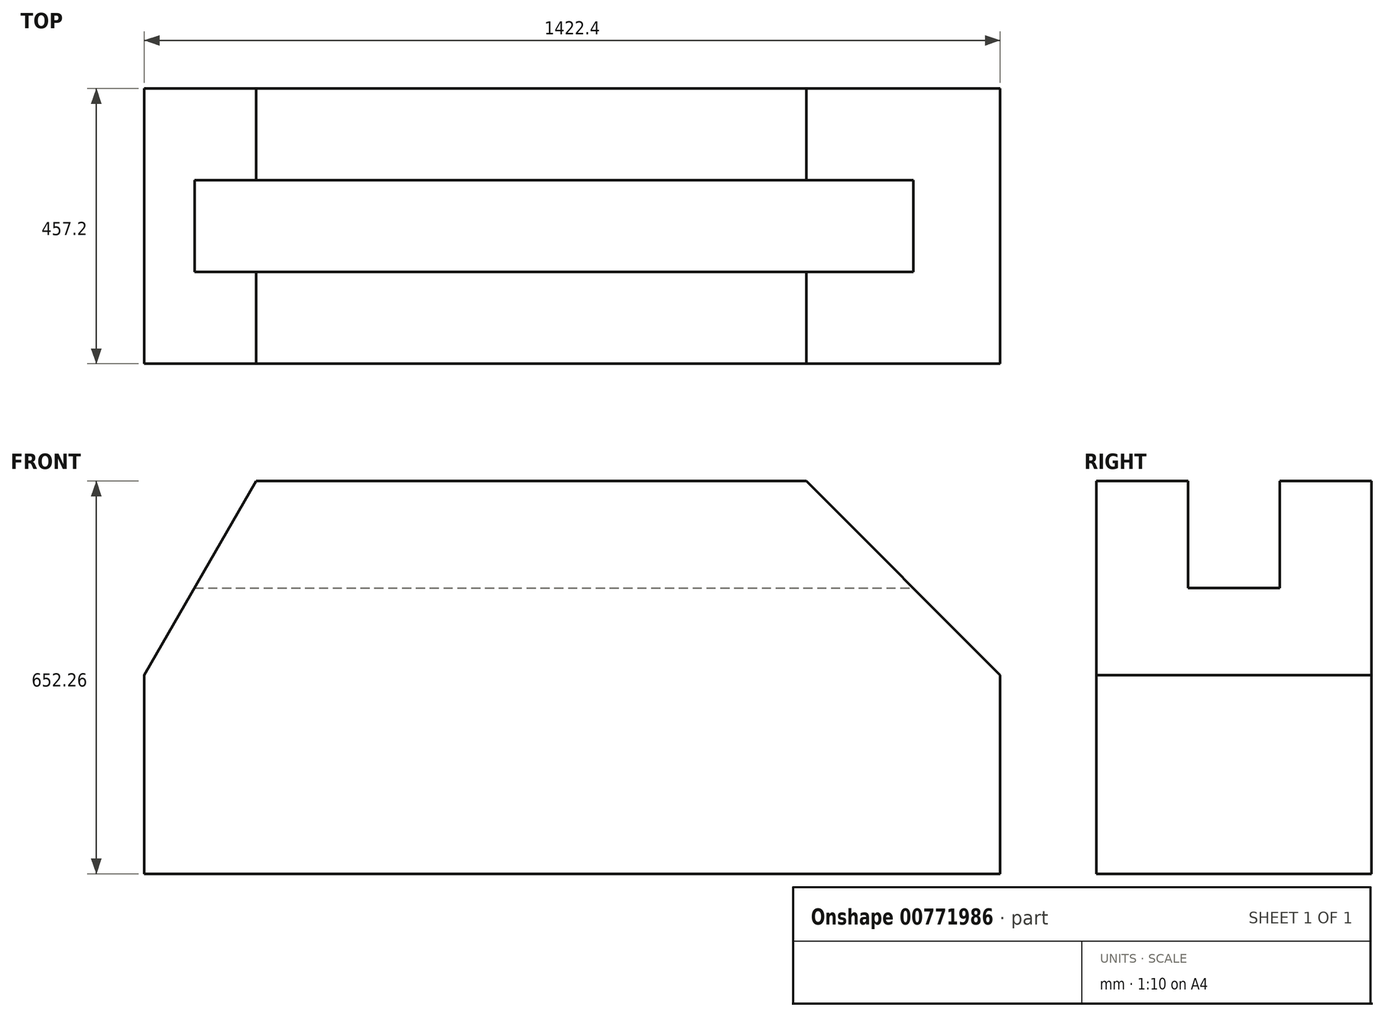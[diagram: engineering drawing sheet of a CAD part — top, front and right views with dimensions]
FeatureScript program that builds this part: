
annotation { "Feature Type Name" : "Feature", "Feature Type Description" : "" }
export const myFeature = defineFeature(function(context is Context, id is Id, definition is map)
    precondition{}
    {
        {
            var Q0;
            Q0=qCreatedBy(makeId("Front.planeOp"),FACE);
            var sketch = newSketch(context, id + "F0", { "sketchPlane" : qUnion([Q0])});
            skLineSegment(sketch, "E0", {"start": v(0, 0) * mm, "end": v(1422.4, 0) * mm});
            skLineSegment(sketch, "E1", {"start": v(1422.4, 0) * mm, "end": v(1422.4, 330.2) * mm});
            skLineSegment(sketch, "E2", {"start": v(1422.4, 330.2) * mm, "end": v(1100.34, 652.26) * mm});
            skLineSegment(sketch, "E3", {"start": v(1100.34, 652.26) * mm, "end": v(185.94, 652.26) * mm});
            skLineSegment(sketch, "E4", {"start": v(185.94, 652.26) * mm, "end": v(0, 330.2) * mm});
            skLineSegment(sketch, "E5", {"start": v(0, 330.2) * mm, "end": v(0, 0) * mm});
            skSolve(sketch);
        }
        {
            var Q0;
            Q0 = qSketchRegion(id + "F0", true);
            extrude(context, id + "F1", {"entities" : qUnion([Q0]), "depth" : 457.2 * mm, "offsetDistance" : 25.4 * mm, "symmetric" : true});
        }
        {
            var Q0;
            Q0=makeQuery(id+"F1.opExtrude","SWEPT_FACE",FACE,{"disambiguationData":[OSD([sQuery(id+"F0.wireOp",EDGE,"E3")])]});
            var sketch = newSketch(context, id + "F2", { "sketchPlane" : qUnion([Q0])});
            skLineSegment(sketch, "E6", {"start": v(-68.06, 76.2) * mm, "end": v(2217.94, 76.2) * mm});
            skLineSegment(sketch, "E7", {"start": v(2217.94, 76.2) * mm, "end": v(2217.94, -76.2) * mm});
            skLineSegment(sketch, "E8", {"start": v(2217.94, -76.2) * mm, "end": v(-68.06, -76.2) * mm});
            skLineSegment(sketch, "E9", {"start": v(-68.06, -76.2) * mm, "end": v(-68.06, 76.2) * mm});
            skSolve(sketch);
        }
        {
            var Q0;
            Q0 = qSketchRegion(id + "F2", true);
            extrude(context, id + "F3", {"entities" : qUnion([Q0]), "operationType" : NewBodyOperationType.REMOVE, "oppositeDirection" : true, "depth" : 177.8 * mm, "offsetDistance" : 25.4 * mm});
        }
    });
